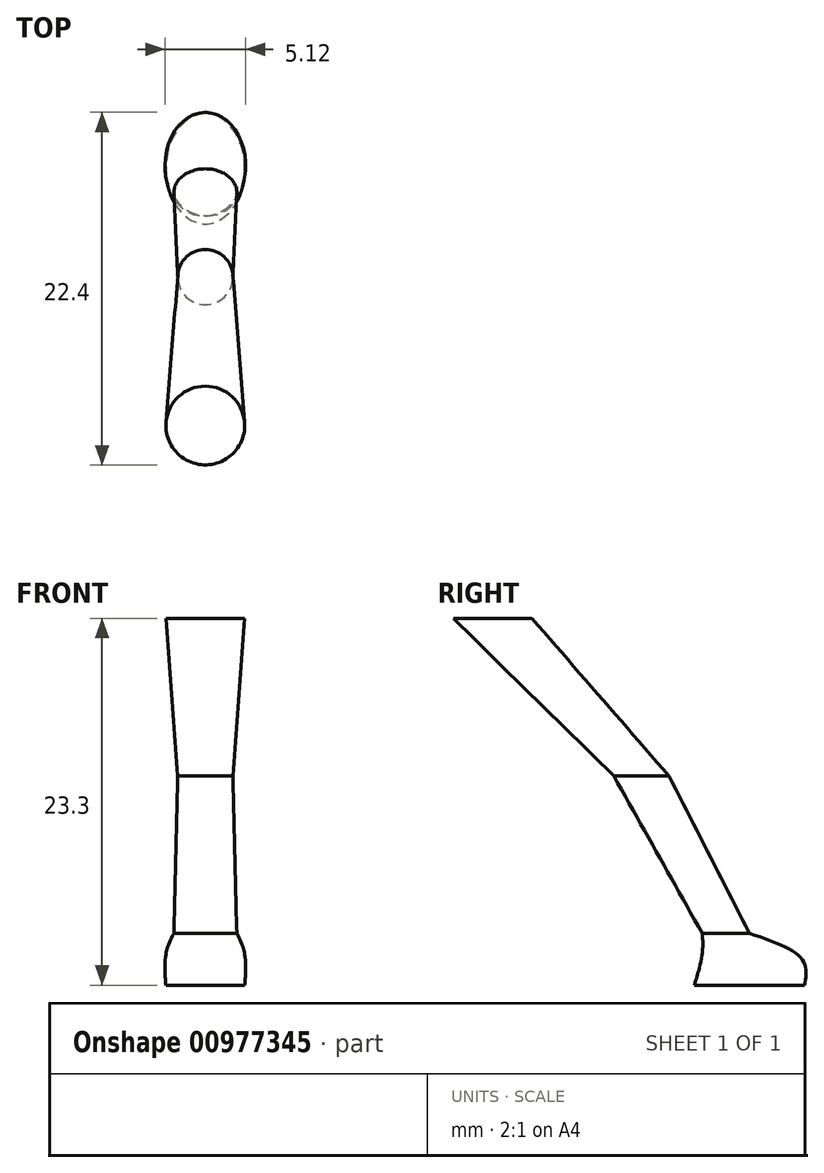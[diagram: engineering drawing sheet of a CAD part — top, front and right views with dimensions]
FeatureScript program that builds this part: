
annotation { "Feature Type Name" : "Feature", "Feature Type Description" : "" }
export const myFeature = defineFeature(function(context is Context, id is Id, definition is map)
    precondition{}
    {
        {
            var Q0;
            Q0=qCreatedBy(makeId("Top.planeOp"),FACE);
            var sketch = newSketch(context, id + "F0", { "sketchPlane" : qUnion([Q0])});
            skEllipse(sketch, "E0", {"center": v(0, 0) * mm, "majorRadius": 2.5 * mm, "minorRadius": 3.5 * mm, "majorAxis": v(1, 0)});
            skSolve(sketch);
        }
        {
            var Q0;
            Q0=qCreatedBy(makeId("Top.planeOp"),FACE);
            cPlane(context, id + "F1", {"entities" : qUnion([Q0]), "cplaneType" : CPlaneType.OFFSET, "offset" : 2 * mm, "width" : 150 * mm, "height" : 150 * mm});
        }
        {
            var Q0;
            Q0=qCreatedBy(id+"F1.planeOp",FACE);
            var sketch = newSketch(context, id + "F2", { "sketchPlane" : qUnion([Q0])});
            skEllipse(sketch, "E1", {"center": v(0, 0) * mm, "majorRadius": 2.5 * mm, "minorRadius": 3 * mm, "majorAxis": v(1, 0)});
            skSolve(sketch);
        }
        {
            var Q0;
            Q0=qCreatedBy(id+"F1.planeOp",FACE);
            cPlane(context, id + "F3", {"entities" : qUnion([Q0]), "cplaneType" : CPlaneType.OFFSET, "offset" : 1.3 * mm, "width" : 150 * mm, "height" : 150 * mm});
        }
        {
            var Q0;
            Q0=qCreatedBy(id+"F3.planeOp",FACE);
            var sketch = newSketch(context, id + "F4", { "sketchPlane" : qUnion([Q0])});
            skEllipse(sketch, "E2", {"center": v(0, -1.5) * mm, "majorRadius": 1.5 * mm, "minorRadius": 2 * mm, "majorAxis": v(0, 1)});
            skSolve(sketch);
        }
        {
            var Q0;
            Q0=makeQuery(id+"F0.imprint","IMPRINT",FACE,{"disambiguationData":[TD([[makeQuery(id+"F0.imprint","IMPRINT",EDGE,{"derivedFrom":sQuery(id+"F0.wireOp",EDGE,"E0")}),1.0]])]});
            var Q1;
            Q1=makeQuery(id+"F2.imprint","IMPRINT",FACE,{"disambiguationData":[TD([[makeQuery(id+"F2.imprint","IMPRINT",EDGE,{"derivedFrom":sQuery(id+"F2.wireOp",EDGE,"E1")}),1.0]])]});
            var Q2;
            Q2=makeQuery(id+"F4.imprint","IMPRINT",FACE,{"disambiguationData":[TD([[makeQuery(id+"F4.imprint","IMPRINT",EDGE,{"derivedFrom":sQuery(id+"F4.wireOp",EDGE,"E2")}),1.0]])]});
            loft(context, id + "F5", {"sheetProfilesArray" : [{ "sheetProfileEntities" : qUnion([Q0]) }, { "sheetProfileEntities" : qUnion([Q1]) }, { "sheetProfileEntities" : qUnion([Q2]) }]});
        }
        {
            var Q0;
            Q0=qCreatedBy(id+"F3.planeOp",FACE);
            cPlane(context, id + "F6", {"entities" : qUnion([Q0]), "cplaneType" : CPlaneType.OFFSET, "offset" : 10 * mm, "width" : 150 * mm, "height" : 150 * mm});
        }
        {
            var Q0;
            Q0=qCreatedBy(id+"F6.planeOp",FACE);
            var sketch = newSketch(context, id + "F7", { "sketchPlane" : qUnion([Q0])});
            skCircle(sketch, "E3", {"center": v(0, -6.87) * mm, "radius": 1.75 * mm});
            skSolve(sketch);
        }
        {
            var Q1;
            Q1=makeQuery(id+"F5.opLoft","CAP_FACE",FACE,{"disambiguationData":[OSD([makeQuery(id+"F4.imprint","IMPRINT",FACE,{"disambiguationData":[TD([[makeQuery(id+"F4.imprint","IMPRINT",EDGE,{"derivedFrom":sQuery(id+"F4.wireOp",EDGE,"E2")}),1.0]])]})])],"isStart":true});
            var Q2;
            Q2=makeQuery(id+"F7.imprint","IMPRINT",FACE,{"disambiguationData":[TD([[makeQuery(id+"F7.imprint","IMPRINT",EDGE,{"derivedFrom":sQuery(id+"F7.wireOp",EDGE,"E3")}),1.0]])]});
            loft(context, id + "F8", {"operationType" : NewBodyOperationType.ADD, "sheetProfilesArray" : [{ "sheetProfileEntities" : qUnion([Q1]) }, { "sheetProfileEntities" : qUnion([Q2]) }]});
        }
        {
            var Q0;
            Q0=qCreatedBy(id+"F6.planeOp",FACE);
            cPlane(context, id + "F9", {"entities" : qUnion([Q0]), "cplaneType" : CPlaneType.OFFSET, "offset" : 10 * mm, "width" : 150 * mm, "height" : 150 * mm});
        }
        {
            var Q0;
            Q0=qCreatedBy(id+"F9.planeOp",FACE);
            var sketch = newSketch(context, id + "F10", { "sketchPlane" : qUnion([Q0])});
            skCircle(sketch, "E4", {"center": v(0, -16.3) * mm, "radius": 2.5 * mm});
            skSolve(sketch);
        }
        {
            var Q1;
            Q1=makeQuery(id+"F8.opLoft","CAP_FACE",FACE,{"disambiguationData":[OSD([makeQuery(id+"F7.imprint","IMPRINT",FACE,{"disambiguationData":[TD([[makeQuery(id+"F7.imprint","IMPRINT",EDGE,{"derivedFrom":sQuery(id+"F7.wireOp",EDGE,"E3")}),1.0]])]})])],"isStart":true});
            var Q2;
            Q2=makeQuery(id+"F10.imprint","IMPRINT",FACE,{"disambiguationData":[TD([[makeQuery(id+"F10.imprint","IMPRINT",EDGE,{"derivedFrom":sQuery(id+"F10.wireOp",EDGE,"E4")}),1.0]])]});
            loft(context, id + "F11", {"operationType" : NewBodyOperationType.ADD, "sheetProfilesArray" : [{ "sheetProfileEntities" : qUnion([Q1]) }, { "sheetProfileEntities" : qUnion([Q2]) }]});
        }
    });
